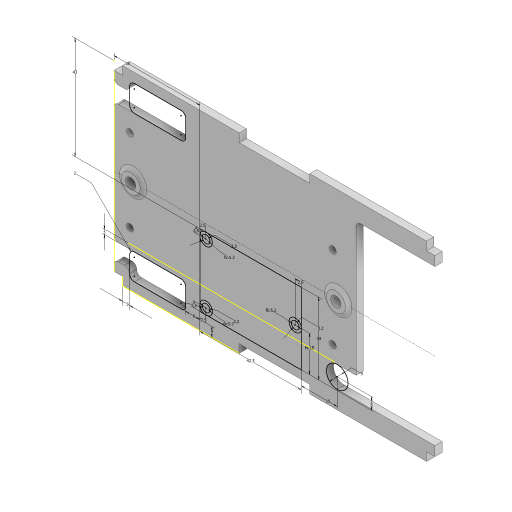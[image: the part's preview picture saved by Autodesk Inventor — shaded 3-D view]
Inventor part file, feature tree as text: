
AUTODESK INVENTOR PART (.ipt)
format: ipt  version: 2023 (Build 270158000, 158)  size: 332,288 bytes
history: native  units: mm
features: extrude x8, sketch x6, fillet x2
ambient origin geometry x8: Origin, YZ Plane, XZ Plane, XY Plane, X Axis, Y Axis, Z Axis, Center Point
bodies: Solid1 (feature_tree)
feature tree (16):
  extrude  "Base Plate"  Depth=80.0mm
  sketch  "Sketch2"  dims[d2=3.5mm d3=3.5mm]
  extrude  "CubePilot Outline"  Depth=3.5mm
  extrude  "Extrusion3"  Depth=3.5mm
  sketch  "Sketch3"  dims[d4=3.5mm d5=3.5mm]
  extrude  "Extrusion6"  Depth=49.0mm
  extrude  "Extrusion7"  Depth=3.5mm
  extrude  "Extrusion8"  Depth=44.29mm
  fillet  "Fillet2"  [1 undecoded]
  extrude  "Extrusion9"  Depth=94.46mm
  fillet  "Fillet3"  Radius=2.0mm
  extrude  "Extrusion10"  Depth=4.0mm
  sketch  "Sketch1"  dims[d0=134.5mm d1=80.0mm]
  sketch  "Sketch6"  dims[d6=49.0mm d7=49.0mm]
  sketch  "Sketch7"  dims[d8=3.5mm d9=3.5mm]
  sketch  "Sketch8"  dims[d10=3.0mm d11=0.0mm d12=44.29mm d13=0.0mm d14=94.46mm d15=2.0mm d16=4.0mm d17=1.0mm d18=2.8mm d19=20.0mm d21=85.0mm d22=20.0mm d24=34.4mm d27=4.73mm d28=4.945mm d29=0.5mm d30=0.0mm d31=0.0mm d32=0.0mm d33=42.5mm d34=30.0mm d35=43.0mm d36=36.0mm d37=3.2mm d38=3.2mm d39=3.2mm d40=2.5mm d41=2.5mm d42=2.5mm d43=2.5mm d44=2.6mm d45=15.0mm d46=9.0mm d47=5.0mm d48=15.0mm d49=3.0mm d50=4.0mm d51=2.0mm d52=6.0mm d53=2.0mm d54=5.2mm d55=5.2mm d56=5.2mm d65=0.0mm d66=0.0mm d67=7.5mm d68=7.5mm d69=0.0mm d70=4.0mm d71=2.0mm d72=0.0mm d73=0.0mm d74=12.0mm d75=5.0mm d76=15.0mm d77=15.0mm d78=6.0mm d79=8.0mm d80=2.0mm d81=8.0mm d82=2.0mm d83=0.0mm d84=0.0mm d85=2.0mm d86=86.0mm d87=8.0mm d88=4.2mm d89=4.2mm d90=8.0mm d91=8.0mm d92=1.0mm d93=0.0mm d94=2.0mm d95=4.2mm d96=4.2mm d97=0.0mm d98=-0.872665mm]
note: 1 required parameter value undecoded (feature->parameter linkage not recoverable at this tier; creation-order binding heuristic only, values carry confidence <= 0.55)
